# Revit family: Sanitary_Wash-basins_hansgrohe_60324XXX-Xuniva-Evo-E-Wash-bowl-400-400
name_source: partatom
category: Plumbing Fixtures
units: mm (PartAtom-declared; Revit-internal decimal feet)

## family parameters
Cut with Voids When Loaded = No
Host = Face
Maintain Annotation Orientation = No
OmniClass Number = 23.31.13.00
OmniClass Title = Sinks
Part Type = Normal
Room Calculation Point = No
Round Connector Dimension = Use Diameter
Shared = No

## types (4) — shared parameters
Connector Description = Water Outlet 31.75mm
Default Elevation = 1219 mm
Description = Xuniva Evo E Wash bowl 400/400 without tap hole and overflow
Diameter = 32 mm
Manufacturer = Hansgrohe
Model = 60324XXX
Product Page URL = https://www.hansgrohe.com
Product data url = https://bimobject.com
URL = https://www.hansgrohe.com
Version = 1

## per-type parameters (varying)
| type | Material |
| 670 Matt Black | Hansgrohe - Ceramic - 670 Matt Black |
| 700 Matt White | Hansgrohe - Ceramic - 700 Matt White |
| 760 Slate Matt Grey | Hansgrohe - Ceramic - 760 Slate Matt Grey |
| 780 Sand Matt Beige | Hansgrohe - Ceramic - 780 Sand Matt Beige |

## geometry (parser evidence)
native form markers: Sweep x3
no freeform markers — native parametric forms only
